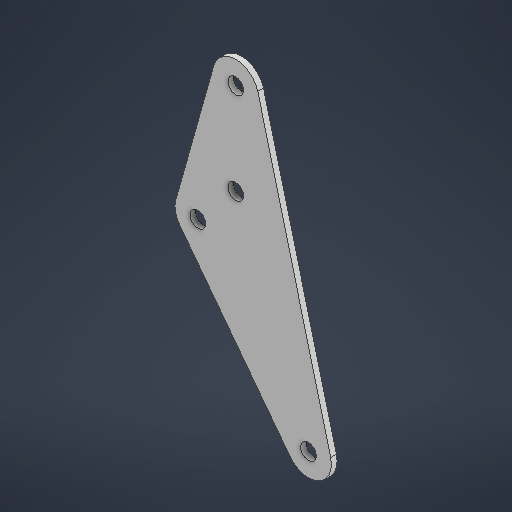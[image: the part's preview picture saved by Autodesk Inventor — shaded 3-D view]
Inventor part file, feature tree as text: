
AUTODESK INVENTOR PART (.ipt)
format: ipt  version: 2025.2 (Build 292293000, 293)  size: 195,584 bytes
history: native  units: in
note: dims shown in document units (in); Inventor stores cm internally (conversion verified against a paired STEP export)
features: extrude x1, sketch x1
ambient origin geometry x8: Origin, YZ Plane, XZ Plane, XY Plane, X Axis, Y Axis, Z Axis, Center Point
bodies: Solid1 (feature_tree)
feature tree (2):
  extrude  "Extrusion1"  Depth=0.0625in TaperAngle=0.0deg
  sketch  "Sketch1"  dims[d0=0.5in d1=0.5in d2=0.5in d3=0.0625in d4=0.0in]
